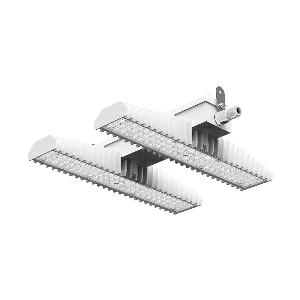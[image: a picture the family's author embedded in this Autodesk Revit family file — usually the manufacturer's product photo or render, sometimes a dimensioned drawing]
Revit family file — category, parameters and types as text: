
# Revit family: 3f_filippi_-_3f_lem_ampio_3f_filippi_-_58900_-_3f_lem_2_led_100_dali_cr_ampio
name_source: partatom
category: Lighting Fixtures
units: mm (PartAtom-declared; Revit-internal decimal feet)

## family parameters
Cut with Voids When Loaded = No
Host = Face
Light Source = No
Part Type = Normal
Room Calculation Point = No
Round Connector Dimension = Use Diameter
Shared = No

## types (1)
- 3F Filippi - 3F LEM Ampio (1 x LED, 16989 lm, 109 W, 4000 K)
    Apparent Load = 109 VA
    Approval mark = CE
    CIE Flux Codes = 60 92 99 100 100
    Color Rendering = 80
    Color Temperature = 4000 K
    Control Gear = Electronic transformer
    Default Elevation = 1800 mm
    Description = Industrial luminaire with high light output and high luminous efficiency designed with the most innovative technologies for environments with temperature up to 55°C.

ILLUMINOTECHNICAL
Luminous efficiency 100% (DLOR 100%, ULOR 0%).
Initial luminous flux of the luminaire 16989 lm.
Direct symmetric wide distribution: the illuminated area has a rectangular shape.
Installation Interdistance Transv.D = 1.58 x hu - Long.D = 1.45 x hu.
Tabular UGR (CIE 117 - 4H-8H; S=0.25H; 70/50/20): RUG 22.5 - 23.5.
Beam angle: 93° - 99°.
Luminous efficacy 156 lm/W.
Lifetime (L93/B10): 30000 h. (tq+25°C)
Lifetime (L90/B10): 50000 h. (tq+25°C)
Lifetime (L85/B10): 80000 h. (tq+25°C)
Lifetime (L80/B10): 100000 h. (tq+25°C)
Lifetime (L85/B10): 50000 h. (tq+55°C)
Sudden decreased luminous flux after 50000 hours: 0% (C0).
Photobiological safety in compliance with IEC/TR 62778: RG0 risk exempt, (IEC 62471).
In compliance with IEC/EN 62722-2-1 - IEC/EN 62717 standards.

SOURCE
2 Mid-Power linear LED modules 50W/840.
Energy efficiency class (UE 2019/2020 - UE 2019/2015): C.
CIE 13.3 Colour rendering index: CRI >80 (R9 <50%).
IES TM-30 Fidelity Index: Rf = 84 Rg = 95.
CCT nominal colour temperature 4000 K.
Colour initial tolerance (MacAdam): SDCM 3.

MECHANICAL
Passive modular heatsinks in die-casted aluminium, painted in white colour.
To optimize the thermal management of the LED module, the heatsinks are oversized and provided with self-cleaning of cooling fins.
Wiring body in aluminium and galvanised steel anchored solidly to the sinks and thermally separated.
3F Lens lenses with high luminous efficiency, transparent methacrylate (PMMA), fixed to the LED modules.
Fixing brackets in stainless steel.
Luminaire with limited surface temperature. - D - (EN 60598-2-24)
Dimensions: 470x542 mm, height 129 mm. Weight 9.21 kg.
IP65 protection degree.
Mechanical strength to impacts IK06 (1 joule).
Glow-wire test resistance 650°C.

ELECTRICAL
Halogen Free DALI-2 DATI (Parts 251, 252, 253), PUSH-DIM, electronic wiring 230V-50/60Hz, power factor 0.97 at full load, THD <25%, constant output current, class I, 1 driver, 1 DALI addresse.
Power of the luminaire 109 W.
ENEC - CE.
Flicker: <4%.
Luminaire compliant with EN 60598-2-22 for power supply from a centralised emergency system CPSS (Central Power Supply System), not incorporated in the luminaire - high risk areas excluded. The default power and flux are 100% in AC and 15% in DC.
Ambient temperature from -30°C to +55°C.
Temperature class T6 max 85°C.
Quick connection via M25 5P connector with 9-13 mm tightening range.
Power unit positioned on a separate compartment by the LED module to ensure optimum temperatures of cabling components, to be inspectable and maintainable.
Relative humidity UR: <85%.

INSTALLATION
Ceiling / Suspended / Wall.
All accessories dedicated to this product are available on the Catalog and on our website www.3F-Filippi.com.

APPLICATIONS
In commercial environments, exhibition and industrial areas, stores, open areas.
Applications with high ambient temperature up to 55°C.
Environments in which it is necessary a total protection against falling fragments (eg environments with foodstuffs or machines with moving parts or with extreme temperature changes), use luminaires with polycarbonate lenses.

LIGHT MANAGEMENT
Recommended minimum setting: 10%.
The luminaire, equipped with (DALI-2 DATI) driver, can be controlled manually with 3F Easy Dim technology or automatically/manually with wired or wireless DALI/D2D control systems.
The D2D driver guarantees interoperability with other devices with the same certification by making the following information available:
Device Data (Part 251), Energy Report (Part 252), Diagnosis & Maintenance (Part 253).
In electrical systems without a regulation system (manual or automatic) and DALI bus, a suitable jumper must be made on the DA-DA terminals of the appliance.

WARNING
Fixture not suitable for cold stores with an ambient temperature <0°C and/or relative humidity >85%.
Luminaire designed for disposal/recycling at end-of-life.
Replaceable (LED only) light source by a professional. Replaceable control gear by a professional.
    Height = 129 mm
    Lamp = 1 x LED
    Lamp Light Flux = 16989 lm
    Lamp Power = 109 W
    Lamp count = 1
    Length = 470 mm
    Lifetime = 50000 h
    Luminous efficacy = 156 lm/W
    Manufacturer = 3F Filippi
    ModVariant = No
    Model = 3F Filippi - 58900 - 3F LEM 2 LED 100 DALI CR AMPIO
    Mounting Place = Ceiling
    Mounting Type = Pendant
    Number of Poles = 1
    OnlyDefault = Yes
    Power Factor = 1
    Product Name = 3F Filippi - 3F LEM Ampio
    Product group = pendant luminaire
    ProductGroupID = 9
    Protection Class = Protection class I
    Protection Degree = IP 65
    RLX_Detail_Level = 1
    RLX_Emergency_Light_Flux = 0 lm
    RLX_Emergency_Type = 0
    RLX_Emergency_Type_DB = No
    RlxData = <blob elided: 98517 chars, md5=cac9efa0>
    Socket = socket
    Standby Power = 0 W
    System Light Flux = 16989 lm
    System Power = 109 W
    Type Comments = Product without accessories
    Type Image = 3f_filippi_-_lem_2.jpg
    URL = http://relux.com
    VarID = ---
    Voltage = 0 V
    Weight = 0.00 kg
    Width = 542 mm

## geometry (parser evidence)
native form markers: Blend x4, Sweep x12
no freeform markers — native parametric forms only
